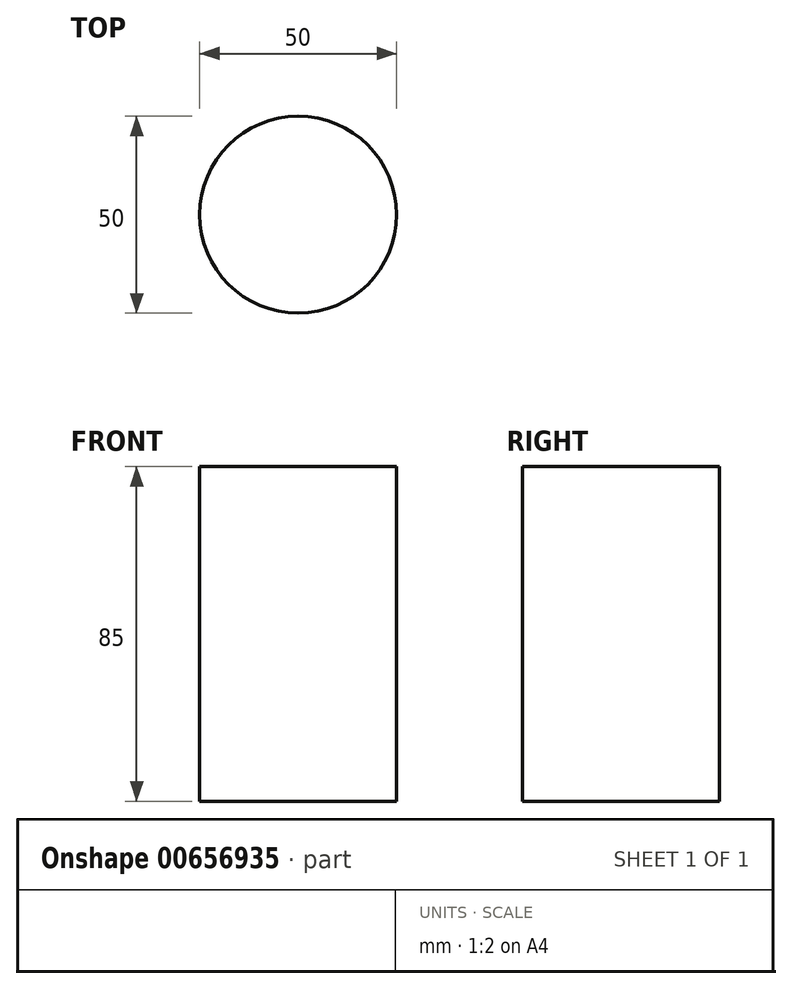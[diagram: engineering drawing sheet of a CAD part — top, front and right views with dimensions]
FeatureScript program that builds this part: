
annotation { "Feature Type Name" : "Feature", "Feature Type Description" : "" }
export const myFeature = defineFeature(function(context is Context, id is Id, definition is map)
    precondition{}
    {
        {
            var Q0;
            Q0=qCreatedBy(makeId("Top.planeOp"),FACE);
            var sketch = newSketch(context, id + "F0", { "sketchPlane" : qUnion([Q0])});
            skCircle(sketch, "E0", {"center": v(0, 0) * mm, "radius": 25 * mm});
            skSolve(sketch);
        }
        {
            var Q0;
            Q0 = qSketchRegion(id + "F0", true);
            extrude(context, id + "F1", {"entities" : qUnion([Q0]), "depth" : 85 * mm, "offsetDistance" : 25 * mm});
        }
    });
